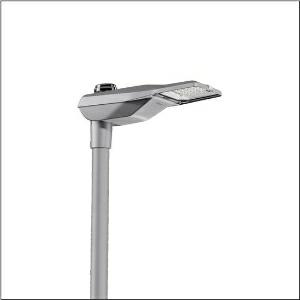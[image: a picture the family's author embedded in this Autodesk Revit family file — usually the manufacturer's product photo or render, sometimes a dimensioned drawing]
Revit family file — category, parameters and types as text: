
# Revit family: streetlight_sl_21_micro___st1_0a_5xe5d37n08cb_defe
name_source: partatom
category: Lighting Fixtures
units: mm (PartAtom-declared; Revit-internal decimal feet)

## family parameters
Cut with Voids When Loaded = No
Host = Face
Light Source = No
Part Type = Normal
Room Calculation Point = No
Round Connector Dimension = Use Diameter
Shared = No

## types (1)
- --- (1 x LED, 2290 lm, 15.8 W, 3000K)
    Apparent Load = 16 VA
    CIE Flux Codes = 37 72 97 100 100
    Color Rendering = 70
    Color Temperature = 3000K
    Default Elevation = 1800 mm
    Description = Streetlight SL 21 micro, mast luminaire, primary light control with lens, of PMMA, primary optical cover: cover, of toughened safety glass, transparent, light distribution: ST1.0a, light emission: direct distribution, primary light characteristic: asymmetric, installation type: post-top, LED, 3G 1.5mm², High Power LED, rated luminous flux: 2.290lm, luminous efficacy: 145lm/W, light colour: 730, colour temperature: 3000K, control gear: NEMA (7pin), control: overheat protection, pre-setting: linear dimming characteristic, constant luminous flux control, time-dependent luminous flux control, flexible luminous flux parameterisation, mains connection: 230..240V, AC, 50/60Hz, connection cable pre-assembled, cable length: 6,5m, wiring characteristics: H07RN-F, start of lifetime: 16W, end of service life: 16W, reduction: 8W, luminaire housing, of diecast aluminium (EN AC-44300), powder-coated, SITECO metallic grey (DB 702S), corrosivity category C5 high according to DIN EN ISO 12944, multi-level sealing system, sealing non-destructively replaceable, inclination adjustable: 0°, 5°, 10°, 15°, length: 528mm, width: 235mm, height: 110mm, spigot size: 76/60mm (post-top), mounting height: 4..8m, protection rating (complete): IP66, insulation class (complete): insulation class I (protective earthing), certification: CE, ENEC, ENEC+, VDE, impact resistance: IK10, permissible operating ambient temperature for outdoor applications: -40..+50°C, standard-compliant lighting for roads and squares, packaging unit: 1 piece

Light Distribution: ST1.0a
    Height = 110 mm
    Lamp = 1 x LED
    Lamp Light Flux = 2290 lm
    Lamp Power = 15.8 W
    Lamp count = 1
    Length = 528 mm
    Luminous efficacy = 145 lm/W
    Manufacturer = Siteco
    ModVariant = No
    Model = 5XE5D37N08CB
    Number of Poles = 1
    OnlyDefault = Yes
    Power Factor = 1
    Product Name = Streetlight SL 21 micro | ST1.0a
    Product group = mast luminaire | pylon top
    ProductGroupID = 6100
    Protection Class = Protection class I
    Protection Degree = IP 66
    RLX_Detail_Level = 1
    RLX_Emergency_Light_Flux = 0 lm
    RLX_Emergency_Type = 0
    RLX_Emergency_Type_DB = No
    RlxData = <blob elided: 98529 chars, md5=e46e9198>
    Socket = socket
    Standby Power = 0 W
    System Light Flux = 2290 lm
    System Power = 16 W
    Type Comments = factory setting: luminous flux: 100 % | dim-lin: 254 | 300 mA
    Type Image = l_1294375.jpg
    URL = http://relux.com
    VarID = @adj_136079
    Voltage = 0 V
    Weight = 0.00 kg
    Width = 235 mm

## geometry (parser evidence)
native form markers: Blend x4, Sweep x13
no freeform markers — native parametric forms only
